# Revit family: Plumbing-Valves-Sloan-CROWN-180z
name_source: partatom
category: Plumbing Fixtures
units: mm (PartAtom-declared; Revit-internal decimal feet)

## family parameters
Cut with Voids When Loaded = No
Host = Face
OmniClass Number = 23.45.05.14.99
OmniClass Title = Other Sanitary Washing Plumbing Fixtures
Part Type = Normal
Room Calculation Point = No
Round Connector Dimension = Use Diameter
Shared = No

## types (2) — shared parameters
Assembly Code = D2020300
CW Connection = Yes
Centerline of Supply from Top of Fixture = 11 1/2"
Centerline of Supply to Centerline of Valve = 4 3/4"
Default Elevation = 0"
Edition number = 1
HW Connection = No
Height = 11 1/2"
Keynote = 15410
Manufacturer = Sloan Valve
Operating Water Pressure = 15 – 80 PSI (103 – 552 kPa)
Product Material = Sloan Valve - Finish - Polished Chrome
Product data url = https://bimobject.com
URL = www.sloanvalve.com
Valve Pressure Drop = 0.00 psi
Vent Connection = No
Waste Connection = No
Water Inlet Connection Diameter = 1"
zero-valued in all types: CWFU, HWFU, WFU

## per-type parameters (varying)
| type | Description | Flush Rate | Part Number |
| CROWN 180-0.5 | 0.5 gpf, Polished Chrome Finish, Fixture Connection Top Spud, Single
Flush, Crown® Exposed Manual Urinal Flushometer. | 0.5 gpf (1.9 Lpf) | 3122420 |
| CROWN 180-1.0 | 1.0 gpf, Polished Chrome Finish, Fixture Connection Top Spud, Single
Flush, Crown® Exposed Manual Urinal Flushometer. | 1.0 gpf (3.8 Lpf) | 3122436 |

note: column(s) folded — value = type name in every type: Model

## geometry (parser evidence)
native form markers: Sweep x6
no freeform markers — native parametric forms only
